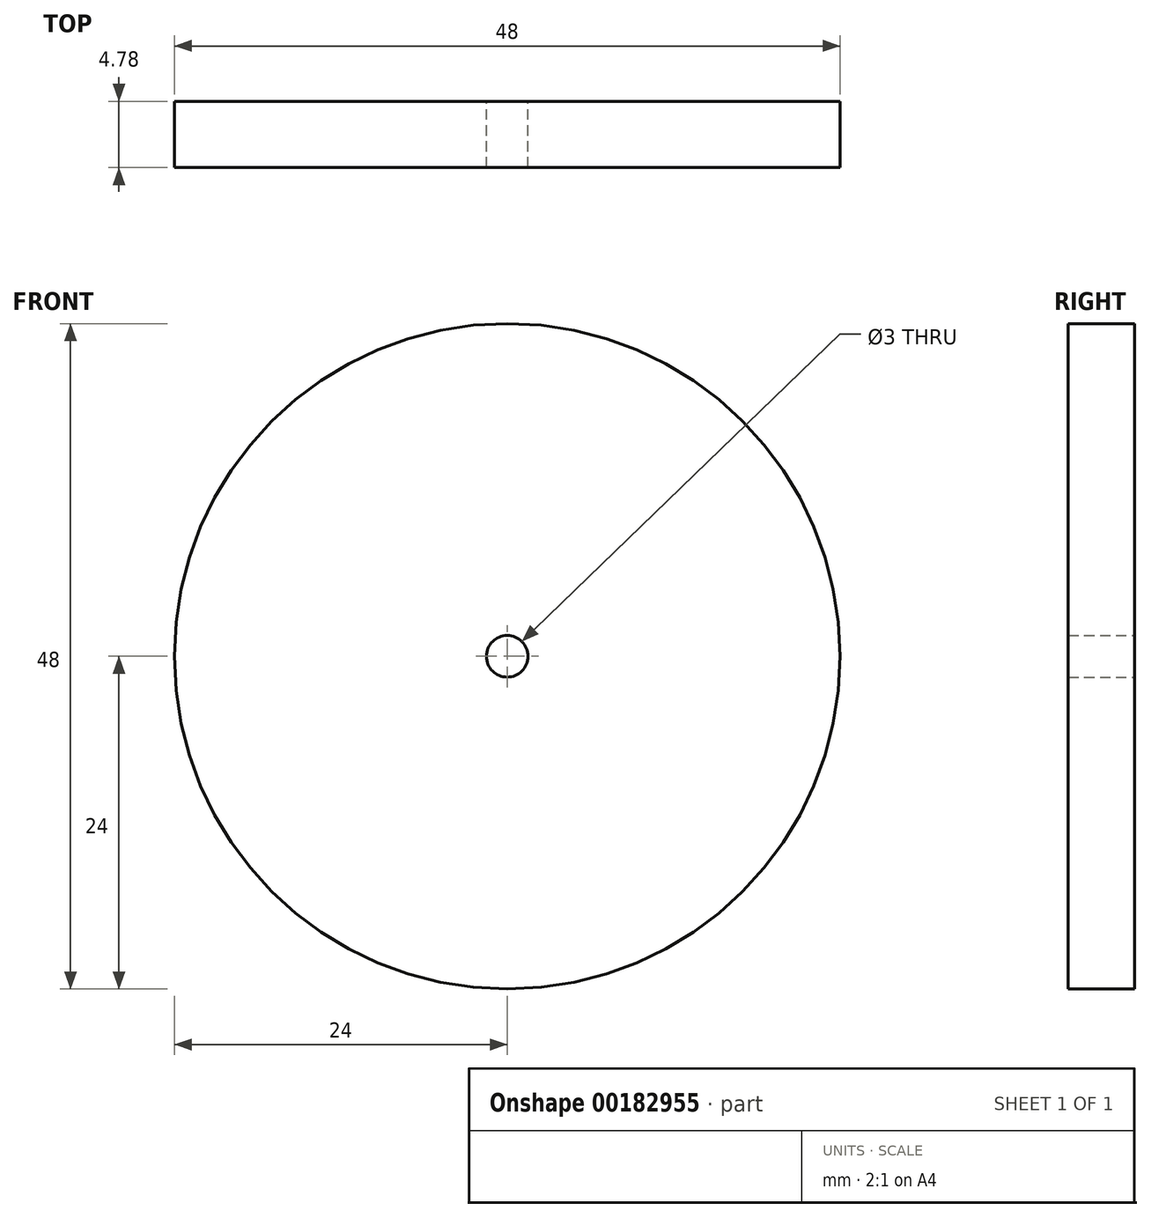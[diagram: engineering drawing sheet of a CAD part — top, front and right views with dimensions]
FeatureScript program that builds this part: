
annotation { "Feature Type Name" : "Feature", "Feature Type Description" : "" }
export const myFeature = defineFeature(function(context is Context, id is Id, definition is map)
    precondition{}
    {
        {
            var Q0;
            Q0=qCreatedBy(makeId("Front.planeOp"),FACE);
            var sketch = newSketch(context, id + "F0", { "sketchPlane" : qUnion([Q0])});
            skCircle(sketch, "E0", {"center": v(0, 0) * mm, "radius": 24 * mm});
            skCircle(sketch, "E1", {"center": v(0, 0) * mm, "radius": 1.5 * mm});
            skSolve(sketch);
        }
        {
            var Q0;
            Q0=makeQuery(id+"F0.imprint","IMPRINT",FACE,{"disambiguationData":[TD([[makeQuery(id+"F0.imprint","IMPRINT",EDGE,{"derivedFrom":sQuery(id+"F0.wireOp",EDGE,"E0")}),1.0]])]});
            var Q1;
            Q1=sQuery(id+"F0.wireOp",EDGE,"E1");
            var Q2;
            Q2=sQuery(id+"F0.wireOp",EDGE,"E0");
            extrude(context, id + "F1", {"entities" : qUnion([Q0]), "surfaceEntities" : qUnion([Q1, Q2]), "depth" : 4.78 * mm});
        }
    });
